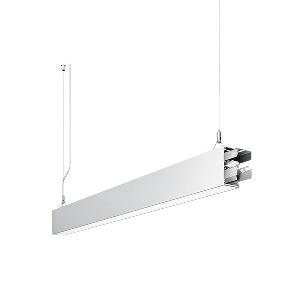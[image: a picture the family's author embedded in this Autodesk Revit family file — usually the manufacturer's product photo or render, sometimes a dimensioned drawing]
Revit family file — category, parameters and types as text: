
# Revit family: dotoo_line_-_dlp_2000_840_d_sta_00805781_2515
name_source: partatom
category: Lighting Fixtures
units: mm (PartAtom-declared; Revit-internal decimal feet)

## family parameters
Cut with Voids When Loaded = No
Host = Face
Light Source = No
Part Type = Normal
Room Calculation Point = No
Round Connector Dimension = Use Diameter
Shared = No

## types (1)
- DOTOO.line - DLP 2000/840/D STA (1 x LED, 1700 lm, 4000K)
    Apparent Load = 16 VA
    Approval mark = CE
    CIE Flux Codes = 67 91 98 100 100
    Color Rendering = 80-89
    Color Temperature = 4000K
    Control Gear = Electronic ballast
    Default Elevation = 1800 mm
    Description = DLP 2000/840/D|Suspended luminaire|light source: LED|connected load: 220-240 V, 50/60 Hz|Power consumption: approx. 16 W|standby: approx. 0,15|luminous flux: 1700 lm|luminous efficacy: 106 lm/W|light distribution: Direct|direct ratio: approx. 100 %|colour temperature: Cold white, ca. 4000 K|color rendering index (CRI): >= 80|chromaticity tolerance:  3 SDCM|System of protection: IP 40|technology: Continuously dimmable|luminaire body|material: Sectional aluminium|colour: White|lamp cover: Acrylic (PMMA), Clear|mains lead: 2.00 m With free stranded wires|Fastening: Steel cable 0.3 - 0.7 m|glare control: Prism aperture|luminance(L65): <= 3000 cd/m|unified glare rating(4H 8H): <=  19|special features: DALI Load 1x, TouchDIM - dimming via standard switch, Through-wired, up to 18 m on one mains connection, Flicker-free, Suitable as emergency lighting, Start luminaire with mains connection, Mechanical and electrical connection of the individual modules without tools|
    Frequency = 50 Hz
    Height = 110 mm
    Lamp = 1 x LED
    Lamp Light Flux = 1700 lm
    Lamp count = 1
    Length = 1408 mm
    Luminous efficacy = 106 lm/W
    Manufacturer = Waldmann
    ModVariant = No
    Model = 00805781
    Mounting Place = Ceiling
    Mounting Type = Pendant
    Number of Poles = 1
    OnlyDefault = Yes
    Power Factor = 1
    Product Name = DOTOO.line - DLP 2000/840/D STA
    Product group = Suspended luminaire
    ProductGroupID = 9
    Protection Class = Protection class I
    Protection Degree = IP 40
    RLX_Detail_Level = 1
    RLX_Emergency_Light_Flux = 0 lm
    RLX_Emergency_Type = 0
    RLX_Emergency_Type_DB = No
    RlxData = <blob elided: 22173 chars, md5=5ee4d17d>
    Socket = socket
    Standby Power = 0 W
    System Light Flux = 1700 lm
    System Power = 16 W
    Type Comments = Product without accessories
    Type Image = 113307000-00692585.jpg
    URL = http://relux.com
    VarID = ---
    Voltage = 230 V
    Voltage Range = 220-240 V
    Weight = 0.00 kg
    Width = 60 mm  [stored 0.19685 ft]

note: [stored X ft] marks values corroborated as IEEE doubles in the binary element streams (Revit-internal decimal feet)

## geometry (parser evidence)
native form markers: Blend x4, Sweep x12
no freeform markers — native parametric forms only
